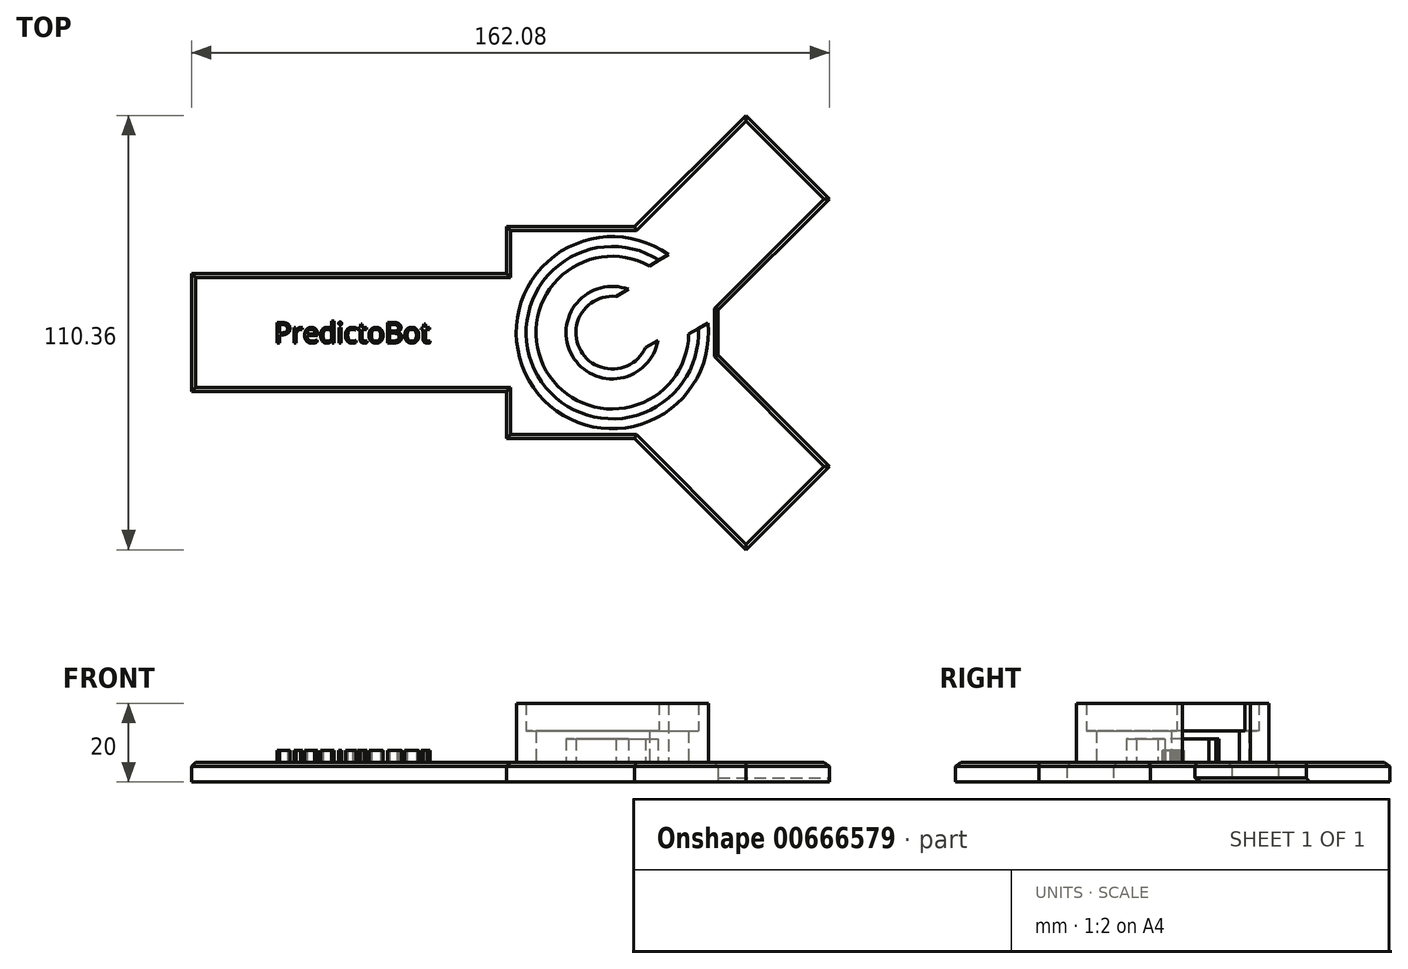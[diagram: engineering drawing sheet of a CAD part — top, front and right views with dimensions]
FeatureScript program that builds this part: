
annotation { "Feature Type Name" : "Feature", "Feature Type Description" : "" }
export const myFeature = defineFeature(function(context is Context, id is Id, definition is map)
    precondition{}
    {
        {
            var Q0;
            Q0=qCreatedBy(makeId("Top.planeOp"),FACE);
            var sketch = newSketch(context, id + "F0", { "sketchPlane" : qUnion([Q0])});
            skLineSegment(sketch, "E0", {"start": v(0, 61.93) * mm, "end": v(0, -68.07) * mm, "construction": true});
            skLineSegment(sketch, "E1", {"start": v(-84.51, 0) * mm, "end": v(85.49, 0) * mm, "construction": true});
            skLineSegment(sketch, "E2.bottom", {"start": v(26.9, -26.9) * mm, "end": v(-26.9, -26.9) * mm});
            skLineSegment(sketch, "E2.top", {"start": v(26.9, 26.9) * mm, "end": v(-26.9, 26.9) * mm});
            skLineSegment(sketch, "E2.left", {"start": v(26.9, -26.9) * mm, "end": v(26.9, 26.9) * mm});
            skLineSegment(sketch, "E2.right", {"start": v(-26.9, -26.9) * mm, "end": v(-26.9, 26.9) * mm});
            skPoint(sketch, "E2.middle", {"position": v(0, 0) * mm});
            skLineSegment(sketch, "E3", {"start": v(-26.9, 15) * mm, "end": v(-106.9, 15) * mm});
            skLineSegment(sketch, "E4.MirrorCS", {"start": v(-26.9, -15) * mm, "end": v(-106.9, -15) * mm});
            skLineSegment(sketch, "E5", {"start": v(-106.9, 15) * mm, "end": v(-106.9, -15) * mm});
            skLineSegment(sketch, "E6", {"start": v(5.7, 26.9) * mm, "end": v(33.97, 55.18) * mm});
            skLineSegment(sketch, "E7", {"start": v(26.9, 5.7) * mm, "end": v(55.18, 33.97) * mm});
            skLineSegment(sketch, "E8", {"start": v(33.97, 55.18) * mm, "end": v(55.18, 33.97) * mm});
            skLineSegment(sketch, "E9.MirrorCS", {"start": v(26.9, -5.7) * mm, "end": v(55.18, -33.97) * mm});
            skLineSegment(sketch, "E10.MirrorCS", {"start": v(33.97, -55.18) * mm, "end": v(55.18, -33.97) * mm});
            skLineSegment(sketch, "E11.MirrorCS", {"start": v(5.7, -26.9) * mm, "end": v(33.97, -55.18) * mm});
            skSolve(sketch);
        }
        {
            var Q0;
            Q0 = qSketchRegion(id + "F0", true);
            extrude(context, id + "F1", {"entities" : qUnion([Q0]), "depth" : 5 * mm, "offsetDistance" : 25 * mm});
        }
        {
            var Q0;
            Q0=makeQuery(id+"F1.opExtrude","CAP_FACE",FACE,{"disambiguationData":[OSD([sQuery(id+"F0.wireOp",EDGE,"E2.bottom"),sQuery(id+"F0.wireOp",EDGE,"E2.top"),sQuery(id+"F0.wireOp",EDGE,"E2.left"),sQuery(id+"F0.wireOp",EDGE,"E2.right"),sQuery(id+"F0.wireOp",EDGE,"E3"),sQuery(id+"F0.wireOp",EDGE,"E4.MirrorCS"),sQuery(id+"F0.wireOp",EDGE,"E5"),sQuery(id+"F0.wireOp",EDGE,"E6"),sQuery(id+"F0.wireOp",EDGE,"E7"),sQuery(id+"F0.wireOp",EDGE,"E8"),sQuery(id+"F0.wireOp",EDGE,"E9.MirrorCS"),sQuery(id+"F0.wireOp",EDGE,"E10.MirrorCS"),sQuery(id+"F0.wireOp",EDGE,"E11.MirrorCS")])],"isStart":false});
            var sketch = newSketch(context, id + "F2", { "sketchPlane" : qUnion([Q0])});
            skCircle(sketch, "E12", {"center": v(0, 0) * mm, "radius": 21.9 * mm});
            skCircle(sketch, "E13", {"center": v(0, 0) * mm, "radius": 24.4 * mm});
            skCircle(sketch, "E14", {"center": v(0, 0) * mm, "radius": 19.4 * mm});
            skLineSegment(sketch, "E15", {"start": v(0, 0) * mm, "end": v(60, 0) * mm, "construction": true});
            skLineSegment(sketch, "E16", {"start": v(0, 0) * mm, "end": v(69.28, 40) * mm, "construction": true});
            skLineSegment(sketch, "E17", {"start": v(9.4, 16.97) * mm, "end": v(14.27, 19.79) * mm});
            skLineSegment(sketch, "E18.MirrorCS", {"start": v(19.4, -0.35) * mm, "end": v(24.27, 2.47) * mm});
            skCircle(sketch, "E19", {"center": v(0, 0) * mm, "radius": 11.75 * mm});
            skCircle(sketch, "E20", {"center": v(0, 0) * mm, "radius": 9.25 * mm});
            skLineSegment(sketch, "E21", {"start": v(0.94, 9.2) * mm, "end": v(4.08, 11.02) * mm});
            skLineSegment(sketch, "E22.MirrorCS", {"start": v(8.44, -3.79) * mm, "end": v(11.58, -1.97) * mm});
            skSolve(sketch);
        }
        {
            var Q0;
            {var subQ0=sQuery(id+"F2.wireOp",EDGE,"E17");var subQ1=sQuery(id+"F2.wireOp",EDGE,"E12");var subQ2=makeQuery(id+"F2.imprint","INTERSECT",VERTEX,{"derivedFrom":[subQ1,subQ0]});Q0=makeQuery(id+"F2.imprint","IMPRINT",FACE,{"disambiguationData":[TD([[makeQuery(id+"F2.imprint","IMPRINT",EDGE,{"disambiguationData":[TD([[subQ2,-1.0]])],"derivedFrom":subQ1}),-1.0]])]});}
            extrude(context, id + "F3", {"entities" : qUnion([Q0]), "operationType" : NewBodyOperationType.ADD, "depth" : 15 * mm, "offsetDistance" : 25 * mm});
        }
        {
            var Q0;
            {var subQ0=sQuery(id+"F2.wireOp",EDGE,"E17");var subQ1=sQuery(id+"F2.wireOp",EDGE,"E12");var subQ2=makeQuery(id+"F2.imprint","INTERSECT",VERTEX,{"derivedFrom":[subQ1,subQ0]});Q0=makeQuery(id+"F2.imprint","IMPRINT",FACE,{"disambiguationData":[TD([[makeQuery(id+"F2.imprint","IMPRINT",EDGE,{"disambiguationData":[TD([[subQ2,-1.0]])],"derivedFrom":subQ1}),1.0]])]});}
            extrude(context, id + "F4", {"entities" : qUnion([Q0]), "operationType" : NewBodyOperationType.ADD, "depth" : 8 * mm, "offsetDistance" : 25 * mm});
        }
        {
            var Q0;
            Q0=makeQuery(id+"F1.opExtrude","CAP_EDGE",EDGE,{"disambiguationData":[OSD([sQuery(id+"F0.wireOp",EDGE,"E4.MirrorCS")])],"isStart":false});
            var Q1;
            Q1=makeQuery(id+"F1.opExtrude","CAP_EDGE",EDGE,{"disambiguationData":[OSD([sQuery(id+"F0.wireOp",EDGE,"E5")])],"isStart":false});
            var Q2;
            Q2=makeQuery(id+"F1.opExtrude","CAP_EDGE",EDGE,{"disambiguationData":[OSD([sQuery(id+"F0.wireOp",EDGE,"E3")])],"isStart":false});
            var Q3;
            {var subQ0=sQuery(id+"F0.wireOp",EDGE,"E2.right");Q3=makeQuery(id+"F1.opExtrude","CAP_EDGE",EDGE,{"disambiguationData":[OSD([subQ0]),TDD([makeQuery(id+"F0.imprint","IMPRINT",EDGE,{"disambiguationData":[TD([[makeQuery(id+"F0.imprint","INTERSECT",VERTEX,{"derivedFrom":[sQuery(id+"F0.wireOp",EDGE,"E2.bottom"),subQ0]}),-1.0]])],"derivedFrom":subQ0})])],"isStart":false});}
            var Q4;
            Q4=makeQuery(id+"F1.opExtrude","CAP_EDGE",EDGE,{"disambiguationData":[OSD([sQuery(id+"F0.wireOp",EDGE,"E2.bottom")])],"isStart":false});
            var Q5;
            Q5=makeQuery(id+"F1.opExtrude","CAP_EDGE",EDGE,{"disambiguationData":[OSD([sQuery(id+"F0.wireOp",EDGE,"E11.MirrorCS")])],"isStart":false});
            var Q6;
            Q6=makeQuery(id+"F1.opExtrude","CAP_EDGE",EDGE,{"disambiguationData":[OSD([sQuery(id+"F0.wireOp",EDGE,"E10.MirrorCS")])],"isStart":false});
            var Q7;
            Q7=makeQuery(id+"F1.opExtrude","CAP_EDGE",EDGE,{"disambiguationData":[OSD([sQuery(id+"F0.wireOp",EDGE,"E9.MirrorCS")])],"isStart":false});
            var Q8;
            Q8=makeQuery(id+"F1.opExtrude","CAP_EDGE",EDGE,{"disambiguationData":[OSD([sQuery(id+"F0.wireOp",EDGE,"E7")])],"isStart":true});
            var Q9;
            Q9=makeQuery(id+"F1.opExtrude","CAP_EDGE",EDGE,{"disambiguationData":[OSD([sQuery(id+"F0.wireOp",EDGE,"E6")])],"isStart":false});
            var Q10;
            Q10=makeQuery(id+"F1.opExtrude","CAP_EDGE",EDGE,{"disambiguationData":[OSD([sQuery(id+"F0.wireOp",EDGE,"E2.top")])],"isStart":false});
            var Q11;
            {var subQ0=sQuery(id+"F0.wireOp",EDGE,"E2.right");Q11=makeQuery(id+"F1.opExtrude","CAP_EDGE",EDGE,{"disambiguationData":[OSD([subQ0]),TDD([makeQuery(id+"F0.imprint","IMPRINT",EDGE,{"disambiguationData":[TD([[makeQuery(id+"F0.imprint","INTERSECT",VERTEX,{"derivedFrom":[sQuery(id+"F0.wireOp",EDGE,"E2.top"),subQ0]}),1.0]])],"derivedFrom":subQ0})])],"isStart":false});}
            var Q12;
            Q12=makeQuery(id+"F1.opExtrude","CAP_EDGE",EDGE,{"disambiguationData":[OSD([sQuery(id+"F0.wireOp",EDGE,"E2.left")])],"isStart":false});
            var Q13;
            Q13=makeQuery(id+"F1.opExtrude","CAP_EDGE",EDGE,{"disambiguationData":[OSD([sQuery(id+"F0.wireOp",EDGE,"E8")])],"isStart":false});
            var Q14;
            Q14=makeQuery(id+"F1.opExtrude","CAP_EDGE",EDGE,{"disambiguationData":[OSD([sQuery(id+"F0.wireOp",EDGE,"E7")])],"isStart":false});
            chamfer(context, id + "F5", {"entities" : qUnion([Q0, Q1, Q2, Q3, Q4, Q5, Q6, Q7, Q8, Q9, Q10, Q11, Q12, Q13, Q14]), "width" : 1 * mm, "tangentPropagation" : true});
        }
        {
            var Q0;
            {var subQ0=sQuery(id+"F2.wireOp",EDGE,"E21");Q0=makeQuery(id+"F2.imprint","IMPRINT",FACE,{"disambiguationData":[TD([[makeQuery(id+"F2.imprint","IMPRINT",EDGE,{"derivedFrom":subQ0}),1.0]])]});}
            extrude(context, id + "F6", {"entities" : qUnion([Q0]), "operationType" : NewBodyOperationType.ADD, "depth" : 6 * mm, "offsetDistance" : 25 * mm});
        }
        {
            var Q0;
            Q0=makeQuery(id+"F1.opExtrude","CAP_FACE",FACE,{"disambiguationData":[OSD([sQuery(id+"F0.wireOp",EDGE,"E2.bottom"),sQuery(id+"F0.wireOp",EDGE,"E2.top"),sQuery(id+"F0.wireOp",EDGE,"E2.left"),sQuery(id+"F0.wireOp",EDGE,"E2.right"),sQuery(id+"F0.wireOp",EDGE,"E3"),sQuery(id+"F0.wireOp",EDGE,"E4.MirrorCS"),sQuery(id+"F0.wireOp",EDGE,"E5"),sQuery(id+"F0.wireOp",EDGE,"E6"),sQuery(id+"F0.wireOp",EDGE,"E7"),sQuery(id+"F0.wireOp",EDGE,"E8"),sQuery(id+"F0.wireOp",EDGE,"E9.MirrorCS"),sQuery(id+"F0.wireOp",EDGE,"E10.MirrorCS"),sQuery(id+"F0.wireOp",EDGE,"E11.MirrorCS")])],"isStart":false});
            var sketch = newSketch(context, id + "F7", { "sketchPlane" : qUnion([Q0])});
            skText(sketch, "E23", { "text": "PredictoBot\n", "fontName": "OpenSans-Regular.ttf"});
            const initialGuessF7  = {"E23": [-0.0859, -0.0026, 1, 0, 0.00522]};
            skSetInitialGuess(sketch, initialGuessF7);
            skSolve(sketch);
        }
        {
            var Q0;
            Q0 = qSketchRegion(id + "F7", true);
            extrude(context, id + "F8", {"entities" : qUnion([Q0]), "operationType" : NewBodyOperationType.ADD, "depth" : 3 * mm, "offsetDistance" : 25 * mm});
        }
    });
